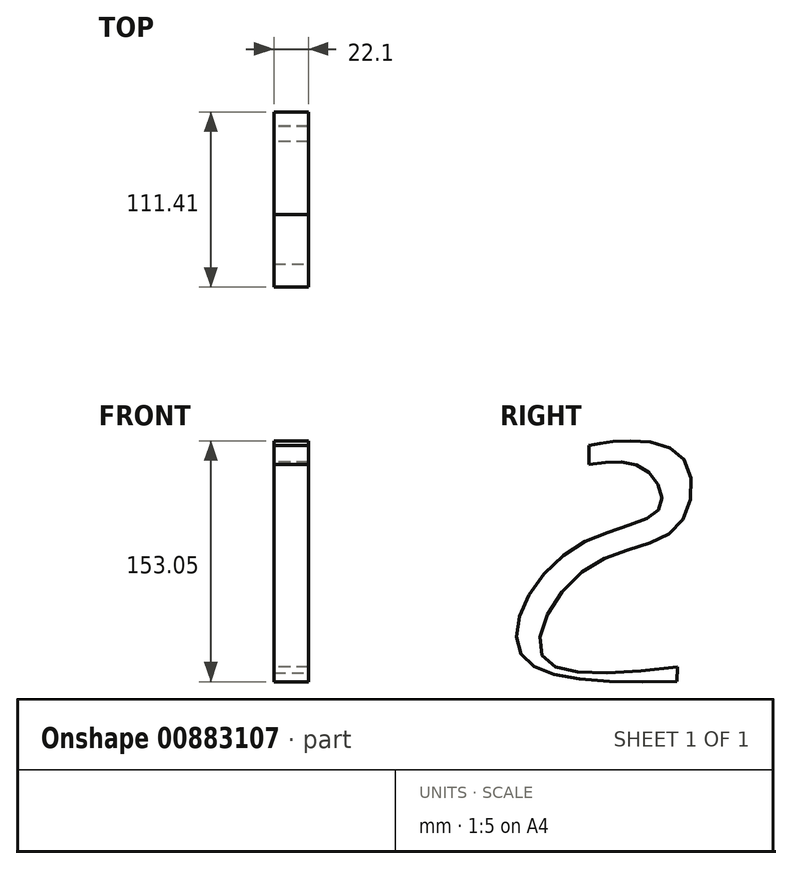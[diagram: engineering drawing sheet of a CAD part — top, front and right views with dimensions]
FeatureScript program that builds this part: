
annotation { "Feature Type Name" : "Feature", "Feature Type Description" : "" }
export const myFeature = defineFeature(function(context is Context, id is Id, definition is map)
    precondition{}
    {
        {
            var Q0;
            Q0=qCreatedBy(makeId("Right.planeOp"),FACE);
            var sketch = newSketch(context, id + "F0", { "sketchPlane" : qUnion([Q0])});
            skFitSpline(sketch, "E0", {"points": [v(-31.04, 70.77) * mm, v(-12.28, 73.53) * mm, v(28.28, 63.32) * mm, v(25.24, 19.17) * mm, v(-31.04, -6.2) * mm, v(-60.84, -62.21) * mm, v(25.24, -69.94) * mm], "startDerivative": vector(152.9, 32.3) * mm, "endDerivative": vector(537.58, 57.5) * mm});
            skLineSegment(sketch, "E1", {"start": v(-31.04, 70.77) * mm, "end": v(-31.04, 58.9) * mm});
            skFitSpline(sketch, "E2", {"points": [v(-31.04, 58.9) * mm, v(4.28, 55.87) * mm, v(13.93, 31.31) * mm, v(-42.07, 4.83) * mm, v(-75.18, -60) * mm, v(24.7, -79.04) * mm], "startDerivative": vector(245.42, 32.59) * mm, "endDerivative": vector(504.43, 6.48) * mm});
            skLineSegment(sketch, "E3", {"start": v(25.24, -69.94) * mm, "end": v(24.7, -79.04) * mm});
            skSolve(sketch);
        }
        {
            var Q0;
            Q0=makeQuery(id+"F0.imprint","IMPRINT",FACE,{"disambiguationData":[TD([[makeQuery(id+"F0.imprint","IMPRINT",EDGE,{"derivedFrom":sQuery(id+"F0.wireOp",EDGE,"E0")}),-1.0]])]});
            extrude(context, id + "F1", {"entities" : qUnion([Q0]), "depth" : 22.1 * mm, "offsetDistance" : 25.4 * mm});
        }
    });
